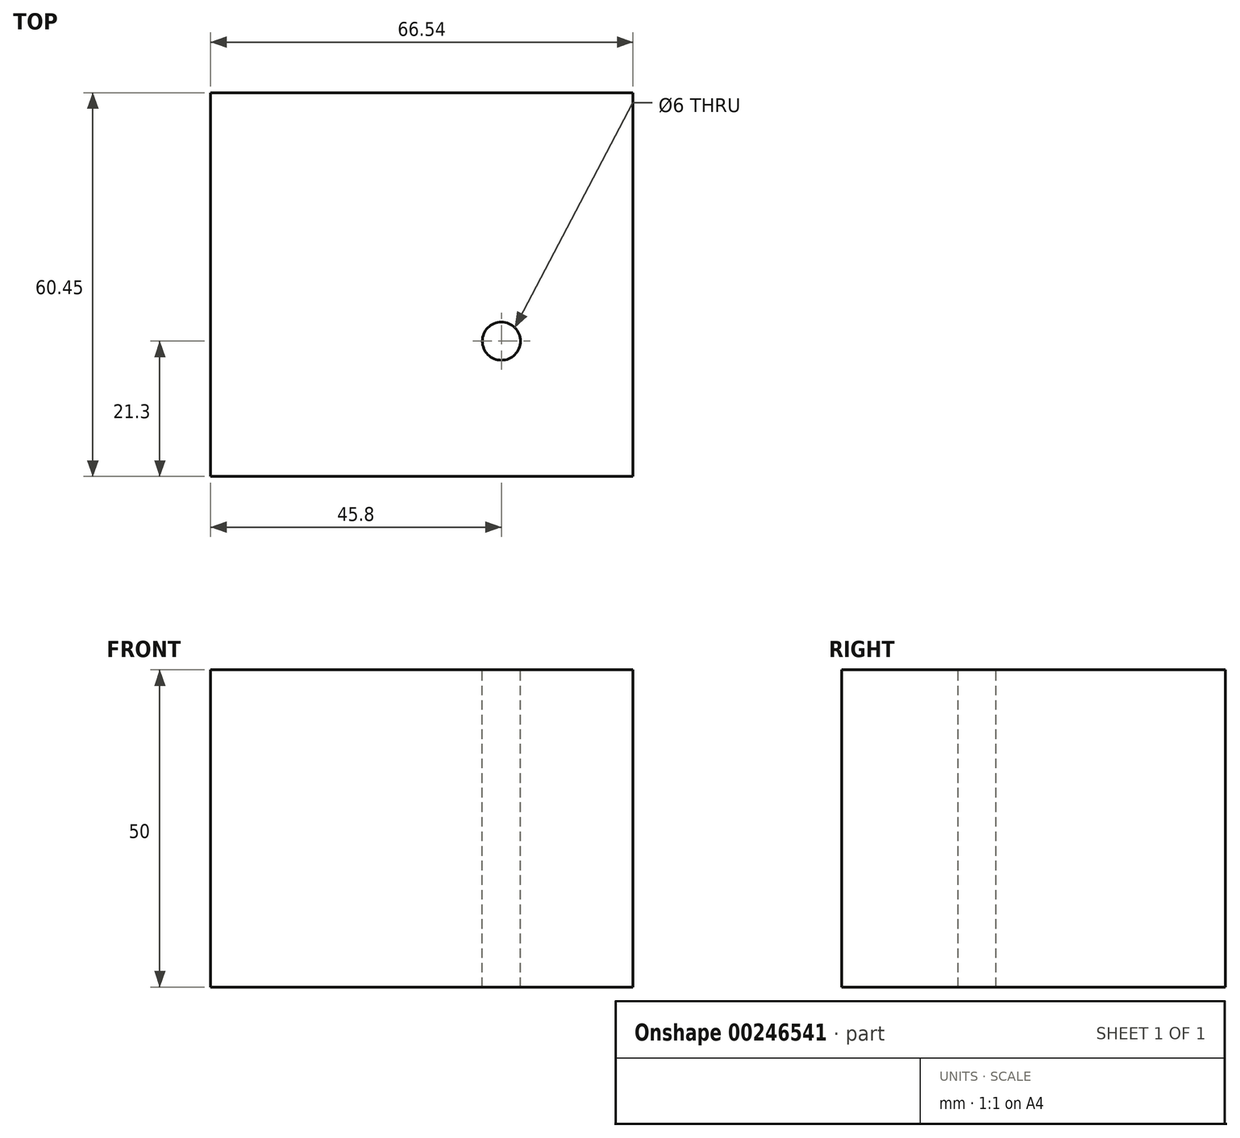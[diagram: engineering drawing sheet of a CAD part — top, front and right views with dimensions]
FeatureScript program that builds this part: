
annotation { "Feature Type Name" : "Feature", "Feature Type Description" : "" }
export const myFeature = defineFeature(function(context is Context, id is Id, definition is map)
    precondition{}
    {
        {
            var Q0;
            Q0=qCreatedBy(makeId("Top.planeOp"),FACE);
            var sketch = newSketch(context, id + "F0", { "sketchPlane" : qUnion([Q0])});
            skLineSegment(sketch, "E0.bottom", {"start": v(20.74, -21.3) * mm, "end": v(-45.8, -21.3) * mm});
            skLineSegment(sketch, "E0.top", {"start": v(20.74, 39.15) * mm, "end": v(-45.8, 39.15) * mm});
            skLineSegment(sketch, "E0.left", {"start": v(20.74, -21.3) * mm, "end": v(20.74, 39.15) * mm});
            skLineSegment(sketch, "E0.right", {"start": v(-45.8, -21.3) * mm, "end": v(-45.8, 39.15) * mm});
            skSolve(sketch);
        }
        {
            var Q0;
            Q0=makeQuery(id+"F0.imprint","IMPRINT",FACE,{"disambiguationData":[TD([[makeQuery(id+"F0.imprint","IMPRINT",EDGE,{"derivedFrom":sQuery(id+"F0.wireOp",EDGE,"E0.bottom")}),-1.0]])]});
            extrude(context, id + "F1", {"entities" : qUnion([Q0]), "depth" : 50 * mm});
        }
        {
            var Q0;
            Q0=makeQuery(id+"F1.opExtrude","CAP_FACE",FACE,{"disambiguationData":[OSD([sQuery(id+"F0.wireOp",EDGE,"E0.bottom"),sQuery(id+"F0.wireOp",EDGE,"E0.top"),sQuery(id+"F0.wireOp",EDGE,"E0.left"),sQuery(id+"F0.wireOp",EDGE,"E0.right")])],"isStart":false});
            var sketch = newSketch(context, id + "F2", { "sketchPlane" : qUnion([Q0])});
            skPoint(sketch, "E1", {"position": v(0, 0) * mm});
            skSolve(sketch);
        }
        {
            var Q0;
            Q0=sQuery(id+"F2.wireOp",VERTEX,"E1");
            var Q1;
            Q1=makeQuery(id+"F1.opExtrude","SWEPT_BODY",BODY,{"disambiguationData":[OSD([sQuery(id+"F0.wireOp",EDGE,"E0.bottom"),sQuery(id+"F0.wireOp",EDGE,"E0.top"),sQuery(id+"F0.wireOp",EDGE,"E0.left"),sQuery(id+"F0.wireOp",EDGE,"E0.right")])]});
            hole(context, id + "F3", {"style" : HoleStyle.SIMPLE, "endStyle" : HoleEndStyle.THROUGH, "holeDiameter" : 6 * mm, "tappedDepth" : 12 * mm, "tapClearance" : 3, "locations" : qUnion([Q0]), "scope" : qUnion([Q1])});
        }
    });
